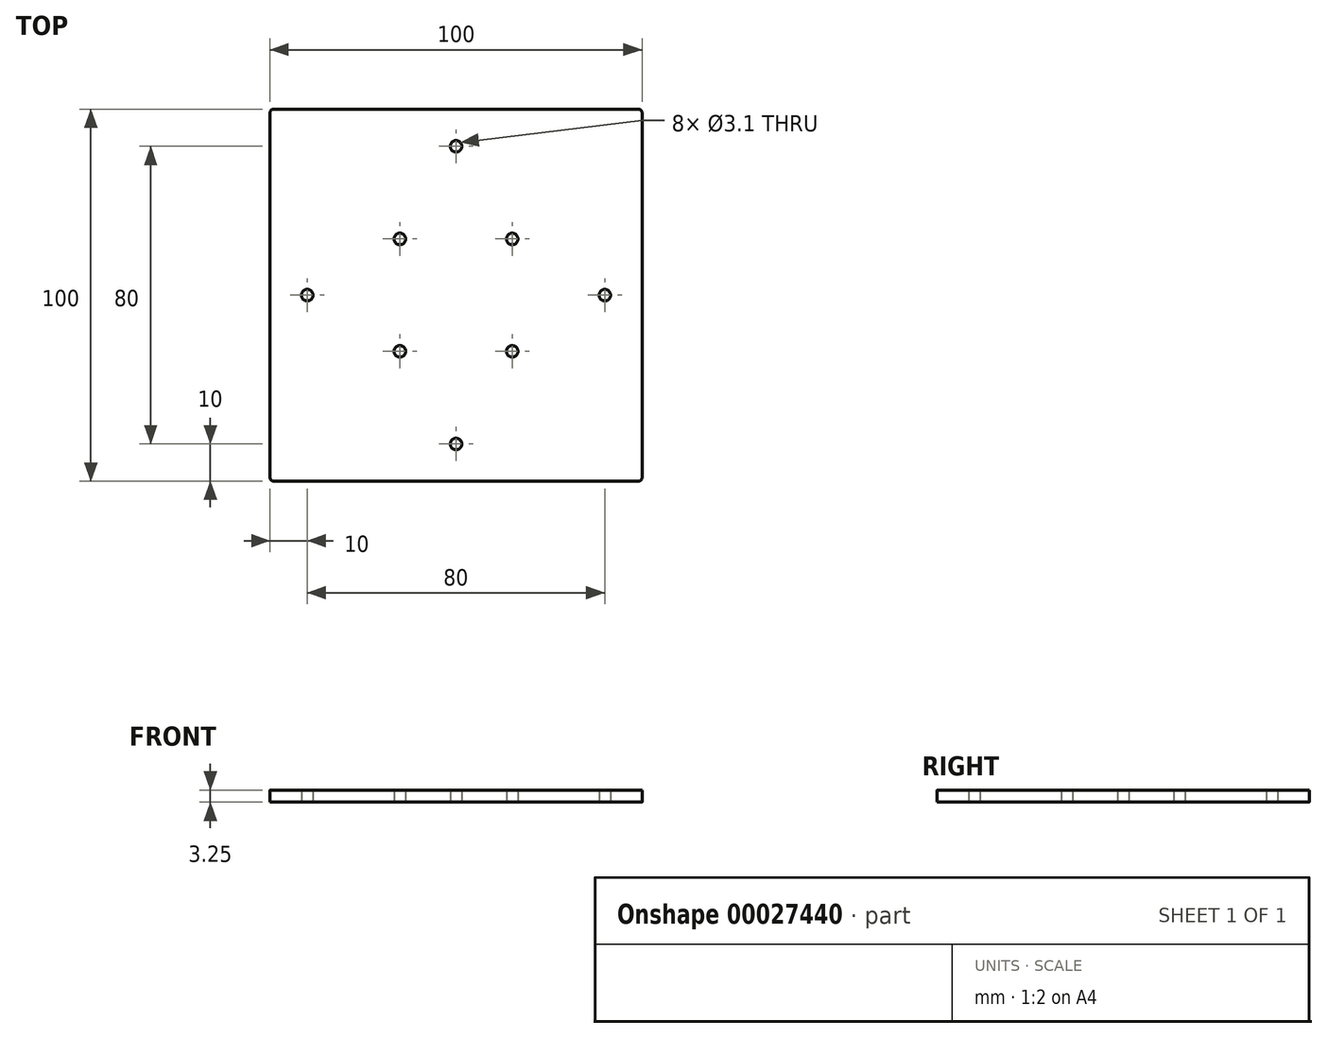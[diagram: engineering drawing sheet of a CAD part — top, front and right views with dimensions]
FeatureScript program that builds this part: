
annotation { "Feature Type Name" : "Feature", "Feature Type Description" : "" }
export const myFeature = defineFeature(function(context is Context, id is Id, definition is map)
    precondition{}
    {
        {
            var Q0;
            Q0=qCreatedBy(makeId("Top.planeOp"),FACE);
            var sketch = newSketch(context, id + "F0", { "sketchPlane" : qUnion([Q0])});
            skLineSegment(sketch, "E0.rect.bottom", {"start": v(-50, 50) * mm, "end": v(50, 50) * mm});
            skLineSegment(sketch, "E0.rect.top", {"start": v(-50, -50) * mm, "end": v(50, -50) * mm});
            skLineSegment(sketch, "E0.rect.left", {"start": v(-50, 50) * mm, "end": v(-50, -50) * mm});
            skLineSegment(sketch, "E0.rect.right", {"start": v(50, 50) * mm, "end": v(50, -50) * mm});
            skLineSegment(sketch, "E1", {"start": v(-50, 0) * mm, "end": v(50, 0) * mm, "construction": true});
            skLineSegment(sketch, "E2", {"start": v(0, 50) * mm, "end": v(0, -50) * mm, "construction": true});
            skPoint(sketch, "E2.endSnap0", {"position": v(0, -50) * mm});
            skCircle(sketch, "E3", {"center": v(-40, 0) * mm, "radius": 1.55 * mm});
            skPoint(sketch, "E4", {"position": v(0, 0) * mm});
            skCircle(sketch, "E5.1.0", {"center": v(0, -40) * mm, "radius": 1.55 * mm});
            skCircle(sketch, "E5.2.0", {"center": v(40, 0) * mm, "radius": 1.55 * mm});
            skCircle(sketch, "E5.3.0", {"center": v(0, 40) * mm, "radius": 1.55 * mm});
            skLineSegment(sketch, "E6", {"start": v(-50, 50) * mm, "end": v(50, -50) * mm, "construction": true});
            skLineSegment(sketch, "E7", {"start": v(50, 50) * mm, "end": v(-50, -50) * mm, "construction": true});
            skCircle(sketch, "E8", {"center": v(-15.1, 15.1) * mm, "radius": 1.55 * mm});
            skCircle(sketch, "E9.1.0", {"center": v(-15.1, -15.1) * mm, "radius": 1.55 * mm});
            skCircle(sketch, "E9.2.0", {"center": v(15.1, -15.1) * mm, "radius": 1.55 * mm});
            skCircle(sketch, "E9.3.0", {"center": v(15.1, 15.1) * mm, "radius": 1.55 * mm});
            skSolve(sketch);
        }
        {
            var Q0;
            Q0 = qSketchRegion(id + "F0", true);
            extrude(context, id + "F1", {"entities" : qUnion([Q0]), "depth" : 3.25 * mm});
        }
        {
            var Q0;
            Q0=makeQuery(id+"F1.opExtrude","SWEPT_EDGE",EDGE,{"disambiguationData":[OSD([sQuery(id+"F0.wireOp",EDGE,"E0.rect.top"),sQuery(id+"F0.wireOp",EDGE,"E0.rect.left")])]});
            var Q1;
            Q1=makeQuery(id+"F1.opExtrude","SWEPT_EDGE",EDGE,{"disambiguationData":[OSD([sQuery(id+"F0.wireOp",EDGE,"E0.rect.top"),sQuery(id+"F0.wireOp",EDGE,"E0.rect.right")])]});
            var Q2;
            Q2=makeQuery(id+"F1.opExtrude","SWEPT_EDGE",EDGE,{"disambiguationData":[OSD([sQuery(id+"F0.wireOp",EDGE,"E0.rect.bottom"),sQuery(id+"F0.wireOp",EDGE,"E0.rect.right")])]});
            var Q3;
            Q3=makeQuery(id+"F1.opExtrude","SWEPT_EDGE",EDGE,{"disambiguationData":[OSD([sQuery(id+"F0.wireOp",EDGE,"E0.rect.bottom"),sQuery(id+"F0.wireOp",EDGE,"E0.rect.left")])]});
            fillet(context, id + "F2", {"entities" : qUnion([Q0, Q1, Q2, Q3]), "radius" : 1 * mm, "tangentPropagation" : true, "allowEdgeOverflow" : false});
        }
    });
